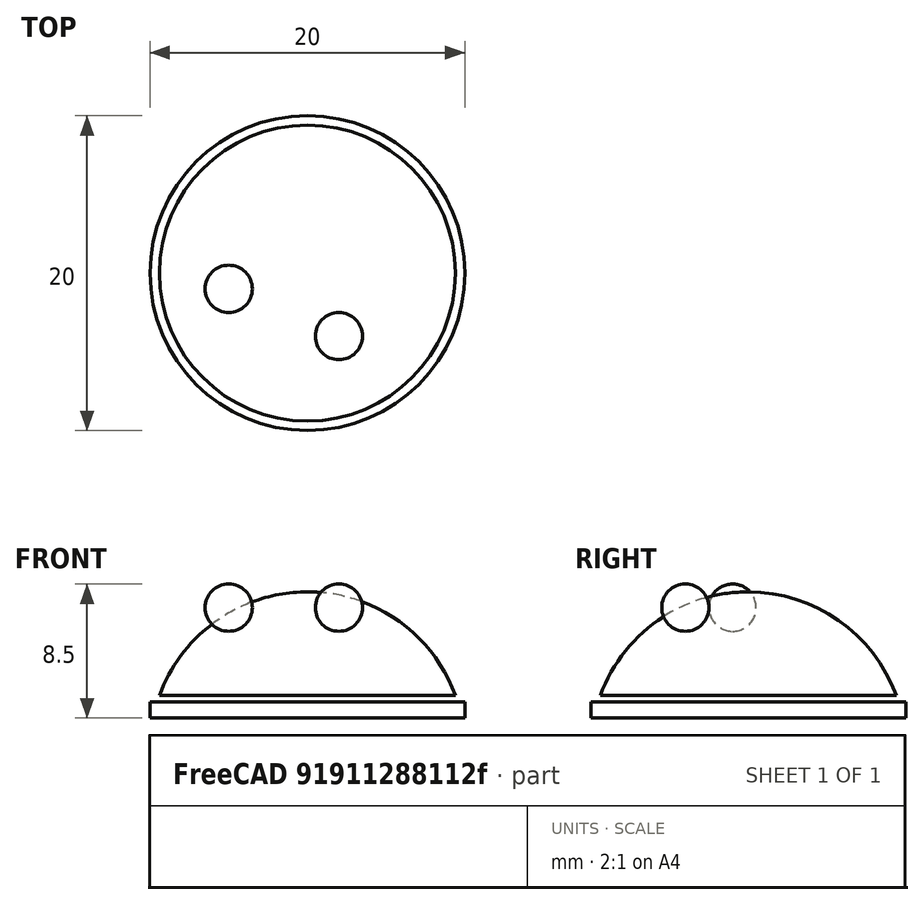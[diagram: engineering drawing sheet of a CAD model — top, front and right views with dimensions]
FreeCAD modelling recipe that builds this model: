
FCSTD DOCUMENT  (FreeCAD 0.20R29177 (Git))
Label: Ejercicio1Video13
License: All rights reserved
LicenseURL: http://en.wikipedia.org/wiki/All_rights_reserved
objects: Part::Sphere×3, Part::Cylinder×1
note: 4 computed .brp shape members not serialized (recipe doc carries the construction recipe); baked Part::Feature solids carry a one-line shape summary decoded from their .brp

FEATURE [Part::Cylinder] Cylinder  label="Cilindro"
  Angle = 360
  AttacherType = Attacher::AttachEngine3D
  FirstAngle = 0
  Height = 1
  Radius = 10
  SecondAngle = 0
FEATURE [Part::Sphere] Sphere  label="Esfera"
  Angle1 = 20
  Angle2 = 90
  Angle3 = 360
  AttacherType = Attacher::AttachEngine3D
  Placement = pos=(0,0,-2) rot=(0,0,1;0rad)
  Radius = 10
FEATURE [Part::Sphere] Sphere001  label="Esfera001"
  Angle1 = -90
  Angle2 = 90
  Angle3 = 360
  AttacherType = Attacher::AttachEngine3D
  Placement = pos=(2,-4,7) rot=(0,0,1;0rad)
  Radius = 1.5
FEATURE [Part::Sphere] Sphere002  label="Esfera002"
  Angle1 = -90
  Angle2 = 90
  Angle3 = 360
  AttacherType = Attacher::AttachEngine3D
  Placement = pos=(-5,-1,7) rot=(0,0,1;0rad)
  Radius = 1.5
